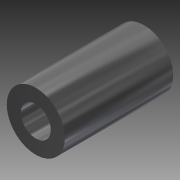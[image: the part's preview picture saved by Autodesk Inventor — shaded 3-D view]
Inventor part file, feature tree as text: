
AUTODESK INVENTOR PART (.ipt)
format: ipt  version: 2012 (Build 160160000, 160)  size: 84,992 bytes
history: native  units: in
note: dims shown in document units (in); Inventor stores cm internally (conversion verified against a paired STEP export)
features: extrude x1, sketch x1
ambient origin geometry x8: Origin, YZ Plane, XZ Plane, XY Plane, X Axis, Y Axis, Z Axis, Center Point
bodies: Solid1 (feature_tree)
feature tree (2):
  extrude  "Extrusion1"  Depth=0.1935in
  sketch  "Sketch1"  dims[d0=0.375in d1=0.1935in d2=0.7in d3=0.0in]
